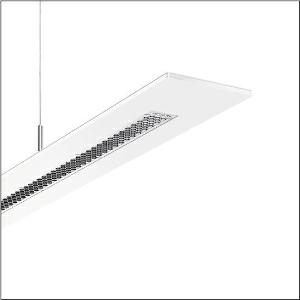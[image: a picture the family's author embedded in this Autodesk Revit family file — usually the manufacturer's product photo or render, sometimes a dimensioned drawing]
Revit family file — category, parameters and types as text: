
# Revit family: arktika_r__21_5mb251dl30830_c5c6
name_source: partatom
category: Lighting Fixtures
units: mm (PartAtom-declared; Revit-internal decimal feet)

## family parameters
Cut with Voids When Loaded = No
Host = Face
Light Source = No
Part Type = Normal
Room Calculation Point = No
Round Connector Dimension = Use Diameter
Shared = No

## types (1)
- --- (1 x LED 3000K / CRI = 80 (unbekannt), 4050 lm, 3000K)
    Apparent Load = 34 VA
    CIE Flux Codes = 81 100 100 79 100
    Color Rendering = 80
    Color Temperature = 3000K
    Default Elevation = 1800 mm
    Description = Arktika® 21, office luminaire, primary anti-glare with honeycomb louvre, of plastic, aluminium vaporised, highly specular, light emission: direct/indirect distribution, primary light characteristic: symmetric, installation type: suspended mounting, LED, rated luminous flux: 4.050lm, luminous efficacy: 120lm/W, light colour: 830, colour temperature: 3000K, control gear: ECG DALI, with terminal, 3+2-pole, max. 2.5mm², mains connection: 220..240V, AC, 50/60Hz, rated input power: 34W, housing, of aluminium, powder-coated, traffic white (RAL 9016), 1-length, length: 1.250mm, width: 120mm, height: 8mm, protection rating (complete): IP20, insulation class (complete): insulation class II (safety insulation), certification: CE, ENEC, VDE, packaging unit: 1 piece
    Height = 8 mm  [stored 0.0262467 ft]
    Lamp = 1 x LED 3000K / CRI >= 80 (unbekannt)
    Lamp Light Flux = 4050 lm
    Lamp count = 1
    Length = 1250 mm
    Luminous efficacy = 120 lm/W
    Manufacturer = Siteco
    ModVariant = No
    Model = 5MB251DL30830
    Mounting Place = Ceiling
    Mounting Type = Pendant
    Number of Poles = 1
    OnlyDefault = Yes
    Power Factor = 1
    Product Name = Arktika® 21
    Product group = office luminaire | ceiling pendant
    ProductGroupID = 902
    Protection Class = Protection class II
    Protection Degree = IP 20
    RLX_Detail_Level = 1
    RLX_Emergency_Light_Flux = 0 lm
    RLX_Emergency_Type = 0
    RLX_Emergency_Type_DB = No
    RlxData = <blob elided: 39341 chars, md5=cf3a0428>
    Socket = socket
    Standby Power = 0 W
    System Light Flux = 4050 lm
    System Power = 34 W
    Type Comments = factory setting: luminous flux: 100 % | dim-lin: 254 | 665 mA
    Type Image = l_1006128.jpg
    URL = http://relux.com
    VarID = @adj_164597
    Voltage = 0 V
    Weight = 0.00 kg
    Width = 120 mm

note: [stored X ft] marks values corroborated as IEEE doubles in the binary element streams (Revit-internal decimal feet)

## geometry (parser evidence)
native form markers: Blend x4, Sweep x12
no freeform markers — native parametric forms only
